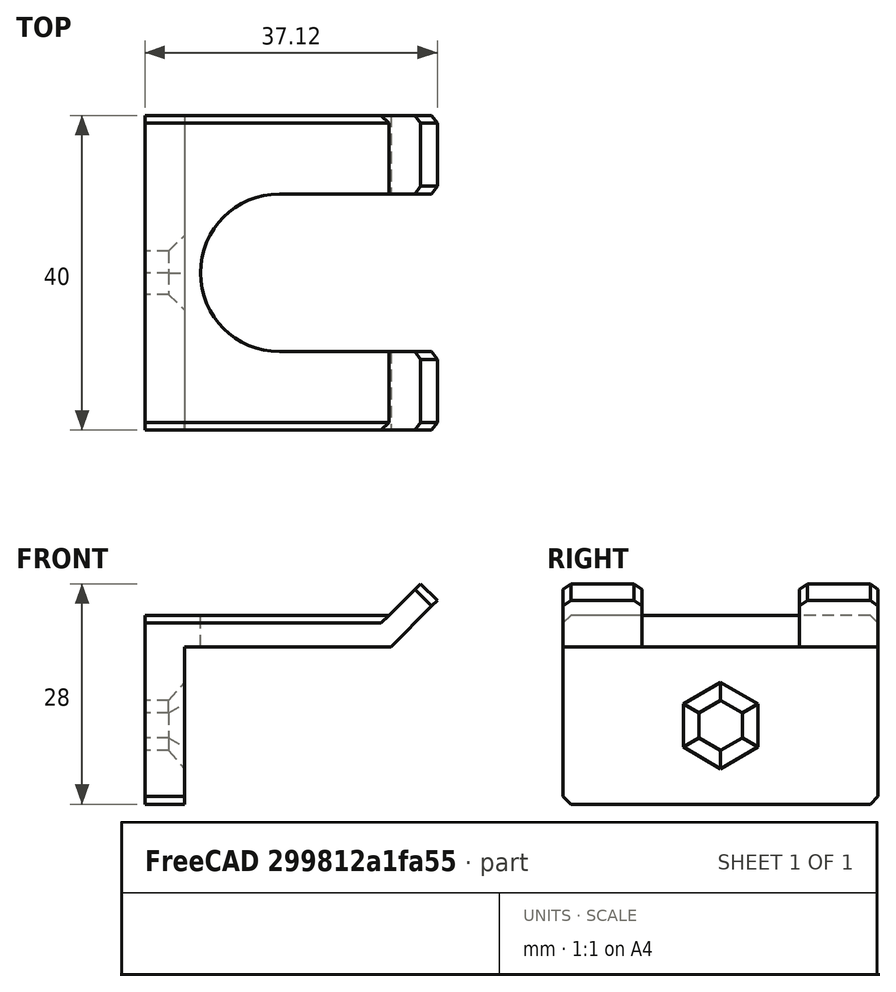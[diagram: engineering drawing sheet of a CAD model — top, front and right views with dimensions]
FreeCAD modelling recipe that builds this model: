
FCSTD DOCUMENT  (FreeCAD 0.19R)
Label: ScaleHolder
License: All rights reserved
LicenseURL: http://en.wikipedia.org/wiki/All_rights_reserved
objects: Sketcher::SketchObject×3, PartDesign::Chamfer×3, PartDesign::Pocket×2, PartDesign::Pad×1, PartDesign::Body×1, Mesh::Feature×1
note: 16 computed .brp shape members not serialized (recipe doc carries the construction recipe); baked Part::Feature solids carry a one-line shape summary decoded from their .brp

FEATURE [Sketcher::SketchObject] Sketch
  FullyConstrained = true
  MapMode = 5
  Placement = pos=(0,0,0) rot=(1,0,0;1.5708rad)
  Support = -> [XZ_Plane]
  sketch-geometry (8):
    g0: LineSegment StartX=0 StartY=4 StartZ=0 EndX=0 EndY=-20 EndZ=0
    g1: LineSegment StartX=0 StartY=-20 StartZ=0 EndX=5 EndY=-20 EndZ=0
    g2: LineSegment StartX=5 StartY=-20 StartZ=0 EndX=5 EndY=0 EndZ=0
    g3: LineSegment StartX=5 StartY=0 StartZ=0 EndX=31.2426 EndY=0 EndZ=0
    g4: LineSegment StartX=31.2426 StartY=0 StartZ=0 EndX=37.1213 EndY=5.87868 EndZ=0
    g5: LineSegment StartX=37.1213 StartY=5.87868 StartZ=0 EndX=35 EndY=8 EndZ=0
    g6: LineSegment StartX=35 StartY=8 StartZ=0 EndX=31 EndY=4 EndZ=0
    g7: LineSegment StartX=31 StartY=4 StartZ=0 EndX=0 EndY=4 EndZ=0
  constraints (24):
    c: PointOnObject(g0,g-2)
    c: PointOnObject(g0,g-2)
    c: Coincident(g0,g1)
    c: Horizontal(g1)
    c: Coincident(g1,g2)
    c: PointOnObject(g2,g-1)
    c: Vertical(g2)
    c: Coincident(g2,g3)
    c: PointOnObject(g3,g-1)
    c: Coincident(g3,g4)
    c: Coincident(g4,g5)
    c: Coincident(g5,g6)
    c: Coincident(g6,g7)
    c: Coincident(g7,g0)
    c: Horizontal(g7)
    c: DistanceX(g5) = 35
    c: Distance(g5) = 3
    c: Angle(g6) = -2.35619
    c: DistanceY(g6) = 4
    c: Parallel(g4,g6)
    c: DistanceX(g2) = 5
    c: Distance(g2) = 20
    c: DistanceY(g5) = 8
    c: Perpendicular(g6,g5)
FEATURE [PartDesign::Pad] Pad
  Direction = (1,1,1)
  Length = 40
  Length2 = 100
  Placement = pos=(0,0,0) rot=(1,0,0;1.5708rad)
  Profile = -> Sketch
  Type = 0
FEATURE [Sketcher::SketchObject] Sketch001
  FullyConstrained = false
  MapMode = 5
  Placement = pos=(0,2.7e-15,4) rot=(0,0,1;3.14159rad)
  Support = -> [Pad]
  sketch-geometry (4):
    g0: ArcOfCircle CenterX=-17.0533 CenterY=20 CenterZ=0 NormalX=0 NormalY=0 NormalZ=1 AngleXU=0 Radius=10 StartAngle=4.71239 EndAngle=7.85398
    g1: ArcOfCircle CenterX=-51.1586 CenterY=20 CenterZ=0 NormalX=0 NormalY=0 NormalZ=1 AngleXU=0 Radius=10 StartAngle=1.5708 EndAngle=4.71239
    g2: LineSegment StartX=-17.0533 StartY=30 StartZ=0 EndX=-51.1586 EndY=30 EndZ=0
    g3: LineSegment StartX=-17.0533 StartY=10 StartZ=0 EndX=-51.1586 EndY=10 EndZ=0
  constraints (8):
    c: Tangent(g0,g3) = 1.5708
    c: Tangent(g0,g2) = -1.5708
    c: Tangent(g2,g1) = -1.5708
    c: Tangent(g3,g1) = 1.5708
    c: Horizontal(g2)
    c: Equal(g0,g1)
    c: Distance(g0,g0) = 20
    c: DistanceY(g0) = 20
FEATURE [PartDesign::Pocket] Pocket
  BaseFeature = -> Pad
  Length = 16
  Length2 = 100
  Midplane = true
  Placement = pos=(0,0,0) rot=(1,0,0;1.5708rad)
  Profile = -> Sketch001
  Type = 0
FEATURE [Sketcher::SketchObject] Sketch002
  FullyConstrained = false
  MapMode = 5
  Placement = pos=(5,0,0) rot=(0.707107,0,0.707107;3.14159rad)
  Support = -> [Pocket]
  sketch-geometry (7):
    g0: LineSegment StartX=-8.42194 StartY=17.25 StartZ=0 EndX=-6.83423 EndY=20 EndZ=0
    g1: LineSegment StartX=-6.83423 StartY=20 StartZ=0 EndX=-8.42194 EndY=22.75 EndZ=0
    g2: LineSegment StartX=-8.42194 StartY=22.75 StartZ=0 EndX=-11.5974 EndY=22.75 EndZ=0
    g3: LineSegment StartX=-11.5974 StartY=22.75 StartZ=0 EndX=-13.1851 EndY=20 EndZ=0
    g4: LineSegment StartX=-13.1851 StartY=20 StartZ=0 EndX=-11.5974 EndY=17.25 EndZ=0
    g5: LineSegment StartX=-11.5974 StartY=17.25 StartZ=0 EndX=-8.42194 EndY=17.25 EndZ=0
    g6: Circle CenterX=-10.0097 CenterY=20 CenterZ=0 NormalX=0 NormalY=0 NormalZ=1 AngleXU=0 Radius=3.17543
  constraints (16):
    c: Coincident(g0,g1)
    c: Coincident(g1,g2)
    c: Coincident(g2,g3)
    c: Coincident(g3,g4)
    c: Coincident(g4,g5)
    c: Coincident(g5,g0)
    c: Equal(g0, g1-g5) x5
    c: PointOnObject(g0,g6)
    c: PointOnObject(g1,g6)
    c: PointOnObject(g2,g6)
    c: PointOnObject(g3,g6)
    c: PointOnObject(g4,g6)
    c: PointOnObject(g5,g6)
    c: Distance(g1,g3) = 5.5
    c: Horizontal(g2)
    c: DistanceY(g6) = 20
FEATURE [PartDesign::Pocket] Pocket001
  BaseFeature = -> Pocket
  Length = 5
  Length2 = 100
  Placement = pos=(0,0,0) rot=(1,0,0;1.5708rad)
  Profile = -> Sketch002
  Type = 0
FEATURE [PartDesign::Chamfer] Chamfer
  Angle = 45
  Base = -> Pocket001 [Edge42,Edge33,Edge35,Edge37,Edge39,Edge41]
  BaseFeature = -> Pocket001
  ChamferType = 0
  FlipDirection = false
  Placement = pos=(0,0,0) rot=(1,0,0;1.5708rad)
  Size = 2
  Size2 = 1
  SupportTransform = false
FEATURE [PartDesign::Chamfer] Chamfer001
  Angle = 45
  Base = -> Chamfer [Edge41,Edge46,Edge34,Edge35]
  BaseFeature = -> Chamfer
  ChamferType = 0
  FlipDirection = false
  Placement = pos=(0,0,0) rot=(1,0,0;1.5708rad)
  Size = 1
  Size2 = 1
  SupportTransform = false
FEATURE [PartDesign::Chamfer] Chamfer002
  Angle = 45
  Base = -> Chamfer001 [Edge38,Edge65,Edge61,Edge31]
  BaseFeature = -> Chamfer001
  ChamferType = 0
  FlipDirection = false
  Placement = pos=(0,0,0) rot=(1,0,0;1.5708rad)
  Size = 1
  Size2 = 1
  SupportTransform = false
FEATURE [PartDesign::Body] Body
  Group = -> [Sketch,Pad,Sketch001,Pocket,Sketch002,Pocket001,Chamfer,Chamfer001,Chamfer002]
  Origin = -> Origin
  Tip = -> Chamfer002
FEATURE [Mesh::Feature] Mesh  label="Chamfer002 (Meshed)"
